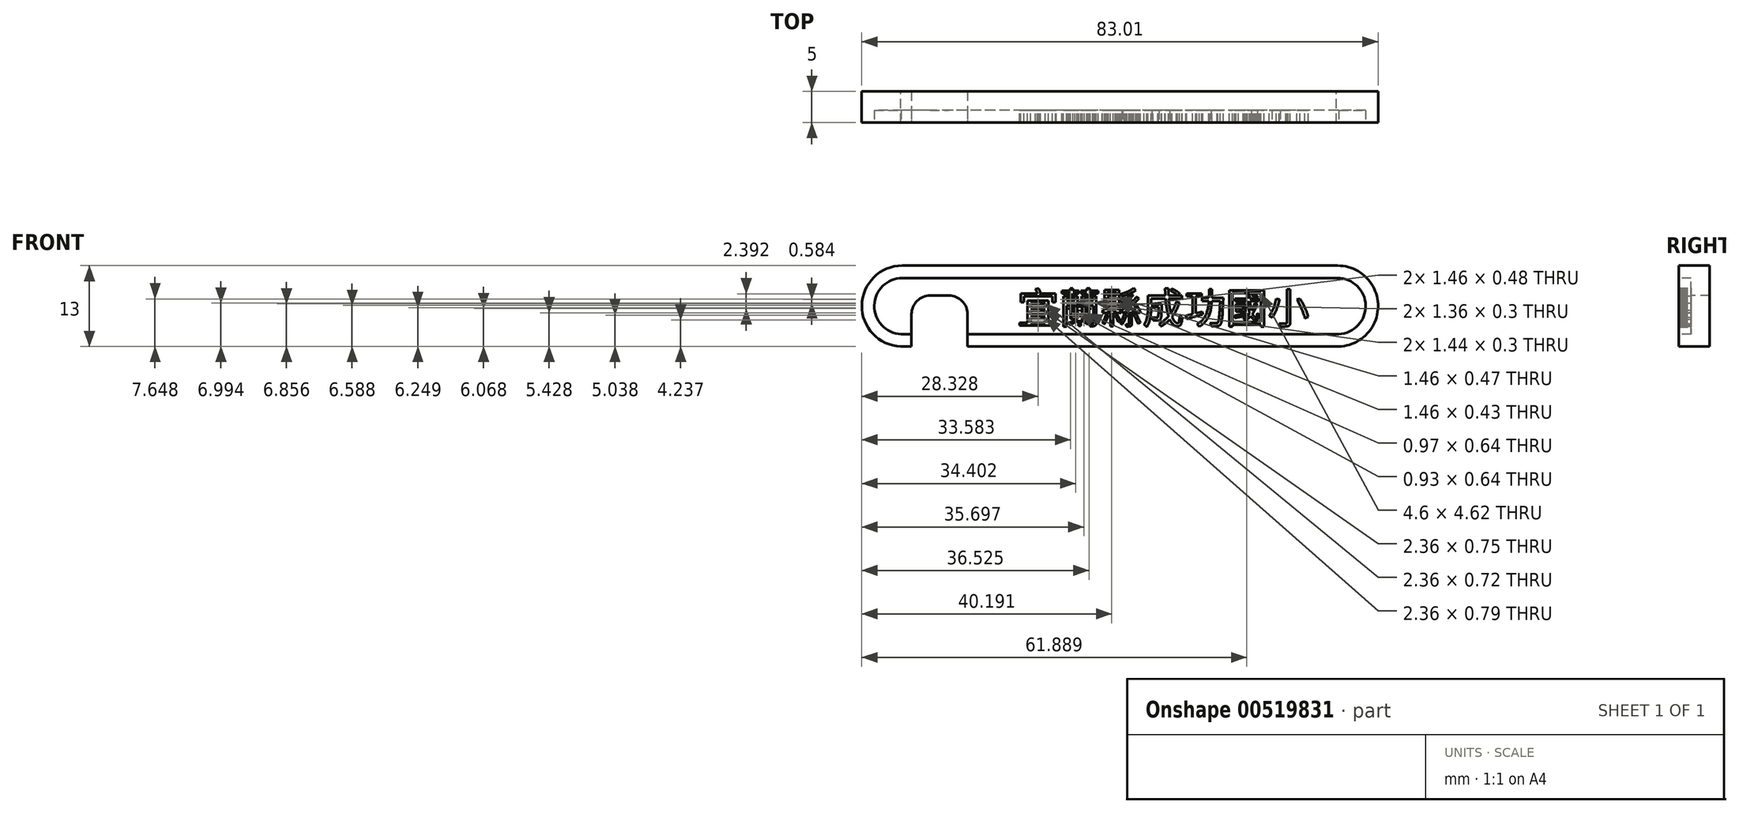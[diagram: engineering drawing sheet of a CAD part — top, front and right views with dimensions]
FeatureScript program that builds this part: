
annotation { "Feature Type Name" : "Feature", "Feature Type Description" : "" }
export const myFeature = defineFeature(function(context is Context, id is Id, definition is map)
    precondition{}
    {
        {
            var Q0;
            Q0=qCreatedBy(makeId("Front.planeOp"),FACE);
            var sketch = newSketch(context, id + "F0", { "sketchPlane" : qUnion([Q0])});
            skLineSegment(sketch, "E0.bottom", {"start": v(34.88, -6.5) * mm, "end": v(-35.12, -6.5) * mm});
            skLineSegment(sketch, "E0.top", {"start": v(35.12, 6.5) * mm, "end": v(-34.88, 6.5) * mm});
            skPoint(sketch, "E0.middle", {"position": v(0, 0) * mm});
            skArc(sketch, "E1", {"start": v(-34.88, 6.5) * mm, "mid": v(-41.39, 0.11) * mm, "end": v(-35.12, -6.5) * mm});
            skArc(sketch, "E2", {"start": v(35.12, 6.5) * mm, "mid": v(41.62, -0.12) * mm, "end": v(34.88, -6.5) * mm});
            skSolve(sketch);
        }
        {
            var Q0;
            Q0=qSketchRegion(id+"F0",true);
            extrude(context, id + "F1", {"entities" : qUnion([Q0]), "depth" : 5 * mm, "offsetDistance" : 25 * mm});
        }
        {
            var Q0;
            Q0=makeQuery(id+"F1.opExtrude","CAP_FACE",FACE,{"disambiguationData":[OSD([sQuery(id+"F0.wireOp",EDGE,"E0.bottom"),sQuery(id+"F0.wireOp",EDGE,"E0.top"),sQuery(id+"F0.wireOp",EDGE,"E1"),sQuery(id+"F0.wireOp",EDGE,"E2")])],"isStart":false});
            var sketch = newSketch(context, id + "F2", { "sketchPlane" : qUnion([Q0])});
            skLineSegment(sketch, "E3.0", {"start": v(35.12, 4.5) * mm, "end": v(-34.88, 4.5) * mm});
            skArc(sketch, "E3.1", {"start": v(35.12, 4.5) * mm, "mid": v(39.62, 0.1) * mm, "end": v(35.3, -4.5) * mm});
            skLineSegment(sketch, "E3.2", {"start": v(35.3, -4.5) * mm, "end": v(-35.08, -4.5) * mm});
            skArc(sketch, "E3.3", {"start": v(-34.88, 4.5) * mm, "mid": v(-39.39, 0.1) * mm, "end": v(-35.08, -4.5) * mm});
            skSolve(sketch);
        }
        {
            var Q0;
            Q0=makeQuery(id+"F2.imprint","IMPRINT",FACE,{"disambiguationData":[TD([[makeQuery(id+"F2.imprint","IMPRINT",EDGE,{"derivedFrom":sQuery(id+"F2.wireOp",EDGE,"E3.0")}),1.0]])]});
            extrude(context, id + "F3", {"entities" : qUnion([Q0]), "operationType" : NewBodyOperationType.REMOVE, "oppositeDirection" : true, "depth" : 2 * mm, "offsetDistance" : 25 * mm});
        }
        {
            var Q0;
            Q0=makeQuery(id+"F1.opExtrude","CAP_FACE",FACE,{"disambiguationData":[OSD([sQuery(id+"F0.wireOp",EDGE,"E0.bottom"),sQuery(id+"F0.wireOp",EDGE,"E0.top"),sQuery(id+"F0.wireOp",EDGE,"E1"),sQuery(id+"F0.wireOp",EDGE,"E2")])],"isStart":false});
            var sketch = newSketch(context, id + "F4", { "sketchPlane" : qUnion([Q0])});
            skLineSegment(sketch, "E4.bottom", {"start": v(-30.39, 1.7) * mm, "end": v(-27.39, 1.7) * mm});
            skLineSegment(sketch, "E4.top", {"start": v(-33.39, -6.5) * mm, "end": v(-24.39, -6.5) * mm});
            skLineSegment(sketch, "E4.left", {"start": v(-33.39, -1.3) * mm, "end": v(-33.39, -6.5) * mm});
            skLineSegment(sketch, "E4.right", {"start": v(-24.39, -1.3) * mm, "end": v(-24.39, -6.5) * mm});
            skPoint(sketch, "E5.visualSharp", {"position": v(-33.39, 1.7) * mm});
            skArc(sketch, "E5.filletArc", {"start": v(-30.39, 1.7) * mm, "mid": v(-32.5, 0.82) * mm, "end": v(-33.39, -1.3) * mm});
            skPoint(sketch, "E6.visualSharp", {"position": v(-24.39, 1.7) * mm});
            skArc(sketch, "E6.filletArc", {"start": v(-24.39, -1.3) * mm, "mid": v(-25.26, 0.82) * mm, "end": v(-27.39, 1.7) * mm});
            skSolve(sketch);
        }
        {
            var Q0;
            Q0=qSketchRegion(id+"F4",true);
            extrude(context, id + "F5", {"entities" : qUnion([Q0]), "operationType" : NewBodyOperationType.REMOVE, "endBound" : BoundingType.THROUGH_ALL, "oppositeDirection" : true, "depth" : 25 * mm, "offsetDistance" : 25 * mm});
        }
        {
            var Q0;
            Q0=makeQuery(id+"F3.boolean.opBoolean","COPY",FACE,{"derivedFrom":makeQuery(id+"F3.opExtrude","CAP_FACE",FACE,{"disambiguationData":[OSD([sQuery(id+"F2.wireOp",EDGE,"E3.0"),sQuery(id+"F2.wireOp",EDGE,"E3.1"),sQuery(id+"F2.wireOp",EDGE,"E3.2"),sQuery(id+"F2.wireOp",EDGE,"E3.3")])],"isStart":false})});
            var sketch = newSketch(context, id + "F6", { "sketchPlane" : qUnion([Q0])});
            skText(sketch, "E7", { "text": "宜蘭縣成功國小", "fontName": "NotoSansCJKtc-Regular.otf"});
            const initialGuessF6  = {"E7": [-0.01639, -0.00279, 1, 0, 0.00483]};
            skSetInitialGuess(sketch, initialGuessF6);
            skSolve(sketch);
        }
        {
            var Q0;
            Q0=qSketchRegion(id+"F6",true);
            extrude(context, id + "F7", {"entities" : qUnion([Q0]), "depth" : 2 * mm, "offsetDistance" : 25 * mm});
        }
        {
            var Q0;
            Q0=makeQuery(id+"F6.imprint","IMPRINT",FACE,{"disambiguationData":[TD([[makeQuery(id+"F6.imprint","IMPRINT",EDGE,{"derivedFrom":sQuery(id+"F6.wireOp",EDGE,"E7.sketch_text.stroke-295")}),1.0]])]});
            extrude(context, id + "F8", {"entities" : qUnion([Q0]), "operationType" : NewBodyOperationType.ADD, "depth" : 2 * mm, "offsetDistance" : 25 * mm});
        }
        {
            var Q0;
            Q0=makeQuery(id+"F6.imprint","IMPRINT",FACE,{"disambiguationData":[TD([[makeQuery(id+"F6.imprint","IMPRINT",EDGE,{"derivedFrom":sQuery(id+"F6.wireOp",EDGE,"E7.sketch_text.stroke-287")}),1.0]])]});
            extrude(context, id + "F9", {"entities" : qUnion([Q0]), "operationType" : NewBodyOperationType.ADD, "depth" : 2 * mm, "offsetDistance" : 25 * mm});
        }
        {
            var Q0;
            Q0=makeQuery(id+"F6.imprint","IMPRINT",FACE,{"disambiguationData":[TD([[makeQuery(id+"F6.imprint","IMPRINT",EDGE,{"derivedFrom":sQuery(id+"F6.wireOp",EDGE,"E7.sketch_text.stroke-283")}),1.0]])]});
            extrude(context, id + "F10", {"entities" : qUnion([Q0]), "operationType" : NewBodyOperationType.ADD, "depth" : 2 * mm, "offsetDistance" : 25 * mm});
        }
        {
            var Q0;
            Q0=makeQuery(id+"F6.imprint","IMPRINT",FACE,{"disambiguationData":[TD([[makeQuery(id+"F6.imprint","IMPRINT",EDGE,{"derivedFrom":sQuery(id+"F6.wireOp",EDGE,"E7.sketch_text.stroke-279")}),1.0]])]});
            extrude(context, id + "F11", {"entities" : qUnion([Q0]), "operationType" : NewBodyOperationType.ADD, "depth" : 2 * mm, "offsetDistance" : 25 * mm});
        }
    });
